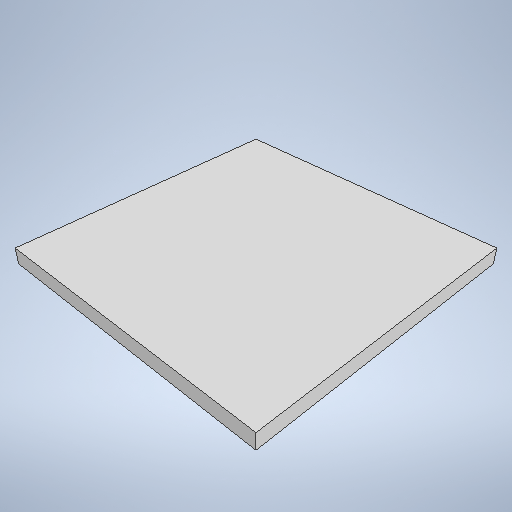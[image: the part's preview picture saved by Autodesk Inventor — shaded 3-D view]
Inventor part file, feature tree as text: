
AUTODESK INVENTOR PART (.ipt)
format: ipt  version: 2025.1 (Build 291241000, 241)  size: 204,800 bytes
history: native  units: mm
features: extrude x1, sketch x1
ambient origin geometry x8: Origin, YZ Plane, XZ Plane, XY Plane, X Axis, Y Axis, Z Axis, Center Point
bodies: Solid1 (feature_tree)
feature tree (2):
  extrude  "Extrusion1"  Depth=350.0mm
  sketch  "Sketch1"  dims[d0=350.0mm d1=350.0mm d2=20.0mm d3=0.0mm]
